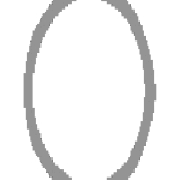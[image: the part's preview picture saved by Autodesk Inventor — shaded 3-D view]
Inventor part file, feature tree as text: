
AUTODESK INVENTOR PART (.ipt)
format: ipt  version: 2021 (Build 250183000, 183)  size: 112,128 bytes
history: native  units: in
note: dims shown in document units (in); Inventor stores cm internally (conversion verified against a paired STEP export)
features: other x4, sketch x3, plane x1
ambient origin geometry x8: Origin, YZ Plane, XZ Plane, XY Plane, X Axis, Y Axis, Z Axis, Center Point
bodies: Solid1 (feature_tree), Body (feature_tree)
feature tree (8):
  other  "Driven Length"
  other  "Frame Generator"
  other  "Start Plane"
  other  "End Plane"
  sketch  "Sketch"  dims[d2=20.0811in d4=-0.0in d5=20.0811in d6=0.12in d7=0.0in d8=90.0deg d9=20.0811in]
  sketch  "Sketch2"  dims[d0=1.0in]
  plane  "Work Plane3"
  sketch  "Sketch3"  dims[d1=0.065in]
